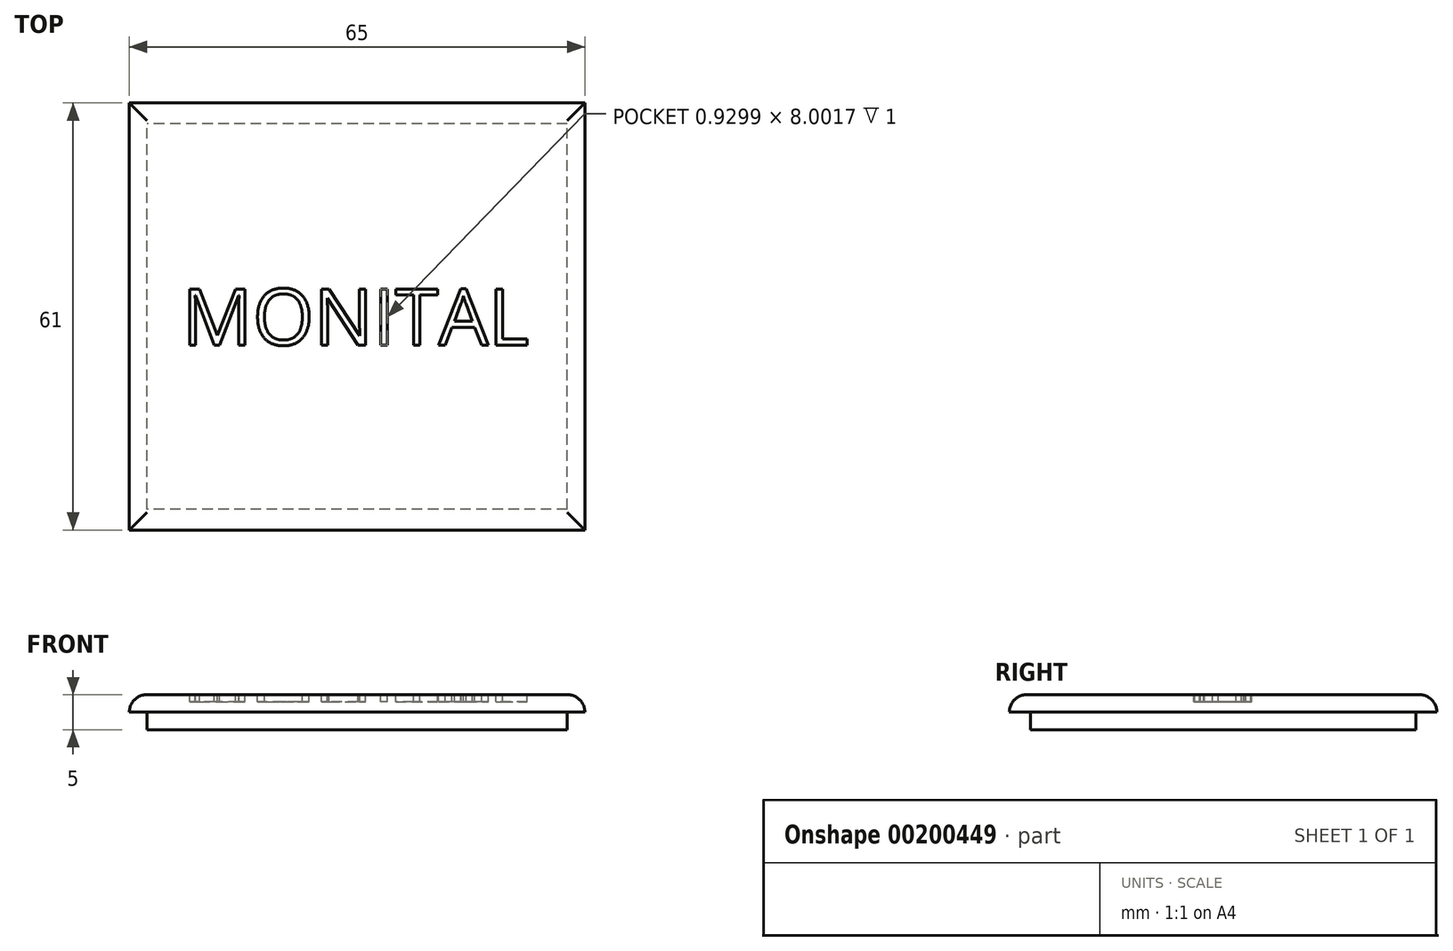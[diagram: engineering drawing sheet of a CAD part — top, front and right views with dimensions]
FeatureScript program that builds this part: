
annotation { "Feature Type Name" : "Feature", "Feature Type Description" : "" }
export const myFeature = defineFeature(function(context is Context, id is Id, definition is map)
    precondition{}
    {
        {
            var Q0;
            Q0=qCreatedBy(makeId("Top.planeOp"),FACE);
            var sketch = newSketch(context, id + "F0", { "sketchPlane" : qUnion([Q0])});
            skLineSegment(sketch, "E0.bottom", {"start": v(32.5, 30.5) * mm, "end": v(-32.5, 30.5) * mm});
            skLineSegment(sketch, "E0.top", {"start": v(32.5, -30.5) * mm, "end": v(-32.5, -30.5) * mm});
            skLineSegment(sketch, "E0.left", {"start": v(32.5, 30.5) * mm, "end": v(32.5, -30.5) * mm});
            skLineSegment(sketch, "E0.right", {"start": v(-32.5, 30.5) * mm, "end": v(-32.5, -30.5) * mm});
            skPoint(sketch, "E0.middle", {"position": v(0, 0) * mm});
            skSolve(sketch);
        }
        {
            var Q0;
            Q0=makeQuery(id+"F0.imprint","IMPRINT",FACE,{"disambiguationData":[TD([[makeQuery(id+"F0.imprint","IMPRINT",EDGE,{"derivedFrom":sQuery(id+"F0.wireOp",EDGE,"E0.bottom")}),1.0]])]});
            extrude(context, id + "F1", {"entities" : qUnion([Q0]), "depth" : 2.5 * mm});
        }
        {
            var Q0;
            Q0=makeQuery(id+"F1.opExtrude","CAP_EDGE",EDGE,{"disambiguationData":[OSD([sQuery(id+"F0.wireOp",EDGE,"E0.top")])],"isStart":false});
            var Q1;
            Q1=makeQuery(id+"F1.opExtrude","CAP_EDGE",EDGE,{"disambiguationData":[OSD([sQuery(id+"F0.wireOp",EDGE,"E0.right")])],"isStart":false});
            var Q2;
            Q2=makeQuery(id+"F1.opExtrude","CAP_EDGE",EDGE,{"disambiguationData":[OSD([sQuery(id+"F0.wireOp",EDGE,"E0.bottom")])],"isStart":false});
            var Q3;
            Q3=makeQuery(id+"F1.opExtrude","CAP_EDGE",EDGE,{"disambiguationData":[OSD([sQuery(id+"F0.wireOp",EDGE,"E0.left")])],"isStart":false});
            fillet(context, id + "F2", {"entities" : qUnion([Q0, Q1, Q2, Q3]), "radius" : 2.5 * mm, "tangentPropagation" : true, "allowEdgeOverflow" : false});
        }
        {
            var Q0;
            Q0=makeQuery(id+"F1.opExtrude","CAP_FACE",FACE,{"disambiguationData":[OSD([sQuery(id+"F0.wireOp",EDGE,"E0.bottom"),sQuery(id+"F0.wireOp",EDGE,"E0.top"),sQuery(id+"F0.wireOp",EDGE,"E0.left"),sQuery(id+"F0.wireOp",EDGE,"E0.right")])],"isStart":false});
            var sketch = newSketch(context, id + "F3", { "sketchPlane" : qUnion([Q0])});
            skText(sketch, "E1", { "text": "MONITAL", "fontName": "OpenSans-Regular.ttf"});
            const initialGuessF3  = {"E1": [-0.025, -0.00407, 1, 0, 0.00807]};
            skSetInitialGuess(sketch, initialGuessF3);
            skSolve(sketch);
        }
        {
            var Q0;
            Q0 = qSketchRegion(id + "F3", true);
            extrude(context, id + "F4", {"entities" : qUnion([Q0]), "operationType" : NewBodyOperationType.REMOVE, "oppositeDirection" : true, "depth" : 1 * mm});
        }
        {
            var Q0;
            Q0=makeQuery(id+"F1.opExtrude","CAP_FACE",FACE,{"disambiguationData":[OSD([sQuery(id+"F0.wireOp",EDGE,"E0.bottom"),sQuery(id+"F0.wireOp",EDGE,"E0.top"),sQuery(id+"F0.wireOp",EDGE,"E0.left"),sQuery(id+"F0.wireOp",EDGE,"E0.right")])],"isStart":true});
            var sketch = newSketch(context, id + "F5", { "sketchPlane" : qUnion([Q0])});
            skLineSegment(sketch, "E2.bottom", {"start": v(30, 27.5) * mm, "end": v(-30, 27.5) * mm});
            skLineSegment(sketch, "E2.top", {"start": v(30, -27.5) * mm, "end": v(-30, -27.5) * mm});
            skLineSegment(sketch, "E2.left", {"start": v(30, 27.5) * mm, "end": v(30, -27.5) * mm});
            skLineSegment(sketch, "E2.right", {"start": v(-30, 27.5) * mm, "end": v(-30, -27.5) * mm});
            skPoint(sketch, "E2.middle", {"position": v(0, 0) * mm});
            skSolve(sketch);
        }
        {
            var Q0;
            Q0 = qSketchRegion(id + "F5", true);
            extrude(context, id + "F6", {"entities" : qUnion([Q0]), "operationType" : NewBodyOperationType.ADD, "depth" : 2.5 * mm});
        }
    });
